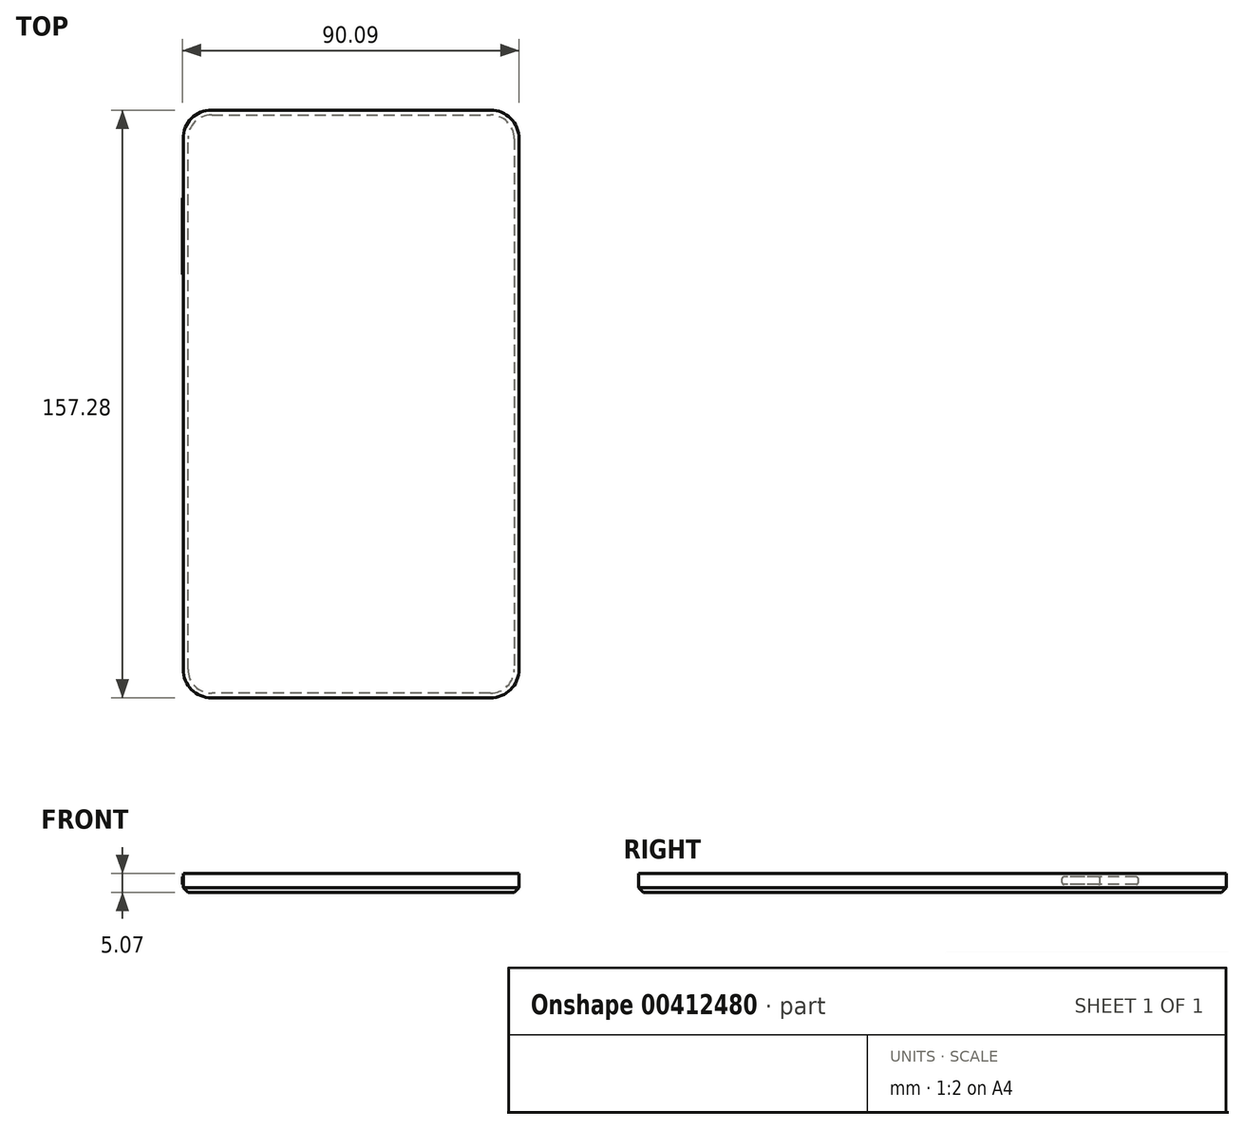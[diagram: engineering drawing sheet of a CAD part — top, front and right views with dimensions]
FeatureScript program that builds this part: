
annotation { "Feature Type Name" : "Feature", "Feature Type Description" : "" }
export const myFeature = defineFeature(function(context is Context, id is Id, definition is map)
    precondition{}
    {
        {
            var Q0;
            Q0=qCreatedBy(makeId("Top.planeOp"),FACE);
            var sketch = newSketch(context, id + "F0", { "sketchPlane" : qUnion([Q0])});
            skLineSegment(sketch, "E0.bottom", {"start": v(44.92, -78.64) * mm, "end": v(-44.92, -78.64) * mm});
            skLineSegment(sketch, "E0.top", {"start": v(44.92, 78.64) * mm, "end": v(-44.92, 78.64) * mm});
            skLineSegment(sketch, "E0.left", {"start": v(44.92, -78.64) * mm, "end": v(44.92, 78.64) * mm});
            skLineSegment(sketch, "E0.right", {"start": v(-44.92, -78.64) * mm, "end": v(-44.92, 78.64) * mm});
            skPoint(sketch, "E0.middle", {"position": v(0, 0) * mm});
            skSolve(sketch);
        }
        {
            var Q0;
            Q0=makeQuery(id+"F0.imprint","IMPRINT",FACE,{"disambiguationData":[TD([[makeQuery(id+"F0.imprint","IMPRINT",EDGE,{"derivedFrom":sQuery(id+"F0.wireOp",EDGE,"E0.bottom")}),-1.0]])]});
            extrude(context, id + "F1", {"entities" : qUnion([Q0]), "depth" : 5.07 * mm});
        }
        {
            var Q0;
            Q0=makeQuery(id+"F1.opExtrude","SWEPT_EDGE",EDGE,{"disambiguationData":[OSD([sQuery(id+"F0.wireOp",EDGE,"E0.bottom"),sQuery(id+"F0.wireOp",EDGE,"E0.right")])]});
            var Q1;
            Q1=makeQuery(id+"F1.opExtrude","SWEPT_EDGE",EDGE,{"disambiguationData":[OSD([sQuery(id+"F0.wireOp",EDGE,"E0.bottom"),sQuery(id+"F0.wireOp",EDGE,"E0.left")])]});
            var Q2;
            Q2=makeQuery(id+"F1.opExtrude","SWEPT_EDGE",EDGE,{"disambiguationData":[OSD([sQuery(id+"F0.wireOp",EDGE,"E0.top"),sQuery(id+"F0.wireOp",EDGE,"E0.left")])]});
            var Q3;
            Q3=makeQuery(id+"F1.opExtrude","SWEPT_EDGE",EDGE,{"disambiguationData":[OSD([sQuery(id+"F0.wireOp",EDGE,"E0.top"),sQuery(id+"F0.wireOp",EDGE,"E0.right")])]});
            fillet(context, id + "F2", {"entities" : qUnion([Q0, Q1, Q2, Q3]), "radius" : 7.62 * mm, "tangentPropagation" : true, "allowEdgeOverflow" : false});
        }
        {
            var Q0;
            Q0=makeQuery(id+"F1.opExtrude","CAP_FACE",FACE,{"disambiguationData":[OSD([sQuery(id+"F0.wireOp",EDGE,"E0.bottom"),sQuery(id+"F0.wireOp",EDGE,"E0.top"),sQuery(id+"F0.wireOp",EDGE,"E0.left"),sQuery(id+"F0.wireOp",EDGE,"E0.right")])],"isStart":true});
            chamfer(context, id + "F3", {"entities" : qUnion([Q0]), "width" : 1.27 * mm, "tangentPropagation" : true});
        }
        {
            var Q0;
            Q0=makeQuery(id+"F1.opExtrude","SWEPT_FACE",FACE,{"disambiguationData":[OSD([sQuery(id+"F0.wireOp",EDGE,"E0.right")])]});
            var sketch = newSketch(context, id + "F4", { "sketchPlane" : qUnion([Q0])});
            skLineSegment(sketch, "E1", {"start": v(90.88, 3.17) * mm, "end": v(-71.02, 3.17) * mm, "construction": true});
            skLineSegment(sketch, "E2.bottom", {"start": v(-55.05, 2.18) * mm, "end": v(-34.65, 2.18) * mm});
            skLineSegment(sketch, "E2.top", {"start": v(-55.05, 4.16) * mm, "end": v(-34.65, 4.16) * mm});
            skLineSegment(sketch, "E2.left", {"start": v(-55.05, 2.18) * mm, "end": v(-55.05, 4.16) * mm});
            skLineSegment(sketch, "E2.right", {"start": v(-34.65, 2.18) * mm, "end": v(-34.65, 4.16) * mm});
            skPoint(sketch, "E2.middle", {"position": v(-44.85, 3.17) * mm});
            skSolve(sketch);
        }
        {
            var Q0;
            Q0 = qSketchRegion(id + "F4", true);
            extrude(context, id + "F5", {"entities" : qUnion([Q0]), "operationType" : NewBodyOperationType.ADD, "depth" : 0.25 * mm});
        }
        {
            var Q0;
            Q0=makeQuery(id+"F5.opExtrude","SWEPT_EDGE",EDGE,{"disambiguationData":[OSD([sQuery(id+"F4.wireOp",EDGE,"E2.top"),sQuery(id+"F4.wireOp",EDGE,"E2.right")])]});
            var Q1;
            Q1=makeQuery(id+"F5.opExtrude","SWEPT_EDGE",EDGE,{"disambiguationData":[OSD([sQuery(id+"F4.wireOp",EDGE,"E2.bottom"),sQuery(id+"F4.wireOp",EDGE,"E2.right")])]});
            var Q2;
            Q2=makeQuery(id+"F5.opExtrude","SWEPT_EDGE",EDGE,{"disambiguationData":[OSD([sQuery(id+"F4.wireOp",EDGE,"E2.top"),sQuery(id+"F4.wireOp",EDGE,"E2.left")])]});
            var Q3;
            Q3=makeQuery(id+"F5.opExtrude","SWEPT_EDGE",EDGE,{"disambiguationData":[OSD([sQuery(id+"F4.wireOp",EDGE,"E2.bottom"),sQuery(id+"F4.wireOp",EDGE,"E2.left")])]});
            fillet(context, id + "F6", {"entities" : qUnion([Q0, Q1, Q2, Q3]), "radius" : 0.5 * mm, "tangentPropagation" : true, "allowEdgeOverflow" : false});
        }
        {
            var Q0;
            Q0=makeQuery(id+"F5.opExtrude","SWEPT_FACE",FACE,{"disambiguationData":[OSD([sQuery(id+"F4.wireOp",EDGE,"E2.top")])]});
            var sketch = newSketch(context, id + "F7", { "sketchPlane" : qUnion([Q0])});
            skLineSegment(sketch, "E3", {"start": v(-45.17, 44.85) * mm, "end": v(-44.4, 44.85) * mm, "construction": true});
            skFitSpline(sketch, "E4", {"points": [v(-45.17, 45.32) * mm, v(-44.99, 44.85) * mm], "startDerivative": vector(0, -1.1) * mm, "endDerivative": vector(0.47, -0.3) * mm});
            skFitSpline(sketch, "E5.MirrorCS", {"points": [v(-45.17, 44.38) * mm, v(-44.99, 44.85) * mm], "startDerivative": vector(0, 1.1) * mm, "endDerivative": vector(0.47, 0.3) * mm});
            skLineSegment(sketch, "E6", {"start": v(-45.17, 45.32) * mm, "end": v(-45.36, 45.32) * mm});
            skLineSegment(sketch, "E7", {"start": v(-45.36, 45.32) * mm, "end": v(-45.4, 44.62) * mm});
            skLineSegment(sketch, "E8", {"start": v(-45.4, 44.62) * mm, "end": v(-45.17, 44.38) * mm});
            skSolve(sketch);
        }
        {
            var Q0;
            {var subQ0=sQuery(id+"F7.wireOp",EDGE,"E6");Q0=makeQuery(id+"F7.imprint","IMPRINT",FACE,{"disambiguationData":[TD([[makeQuery(id+"F7.imprint","IMPRINT",EDGE,{"derivedFrom":subQ0}),1.0]])]});}
            var Q1;
            {var subQ0=sQuery(id+"F7.wireOp",EDGE,"E4");Q1=makeQuery(id+"F7.imprint","IMPRINT",FACE,{"disambiguationData":[TD([[makeQuery(id+"F7.imprint","IMPRINT",EDGE,{"derivedFrom":subQ0}),-1.0]])]});}
            extrude(context, id + "F8", {"entities" : qUnion([Q0, Q1]), "operationType" : NewBodyOperationType.REMOVE, "endBound" : BoundingType.THROUGH_ALL, "oppositeDirection" : true, "depth" : 25.4 * mm});
        }
    });
